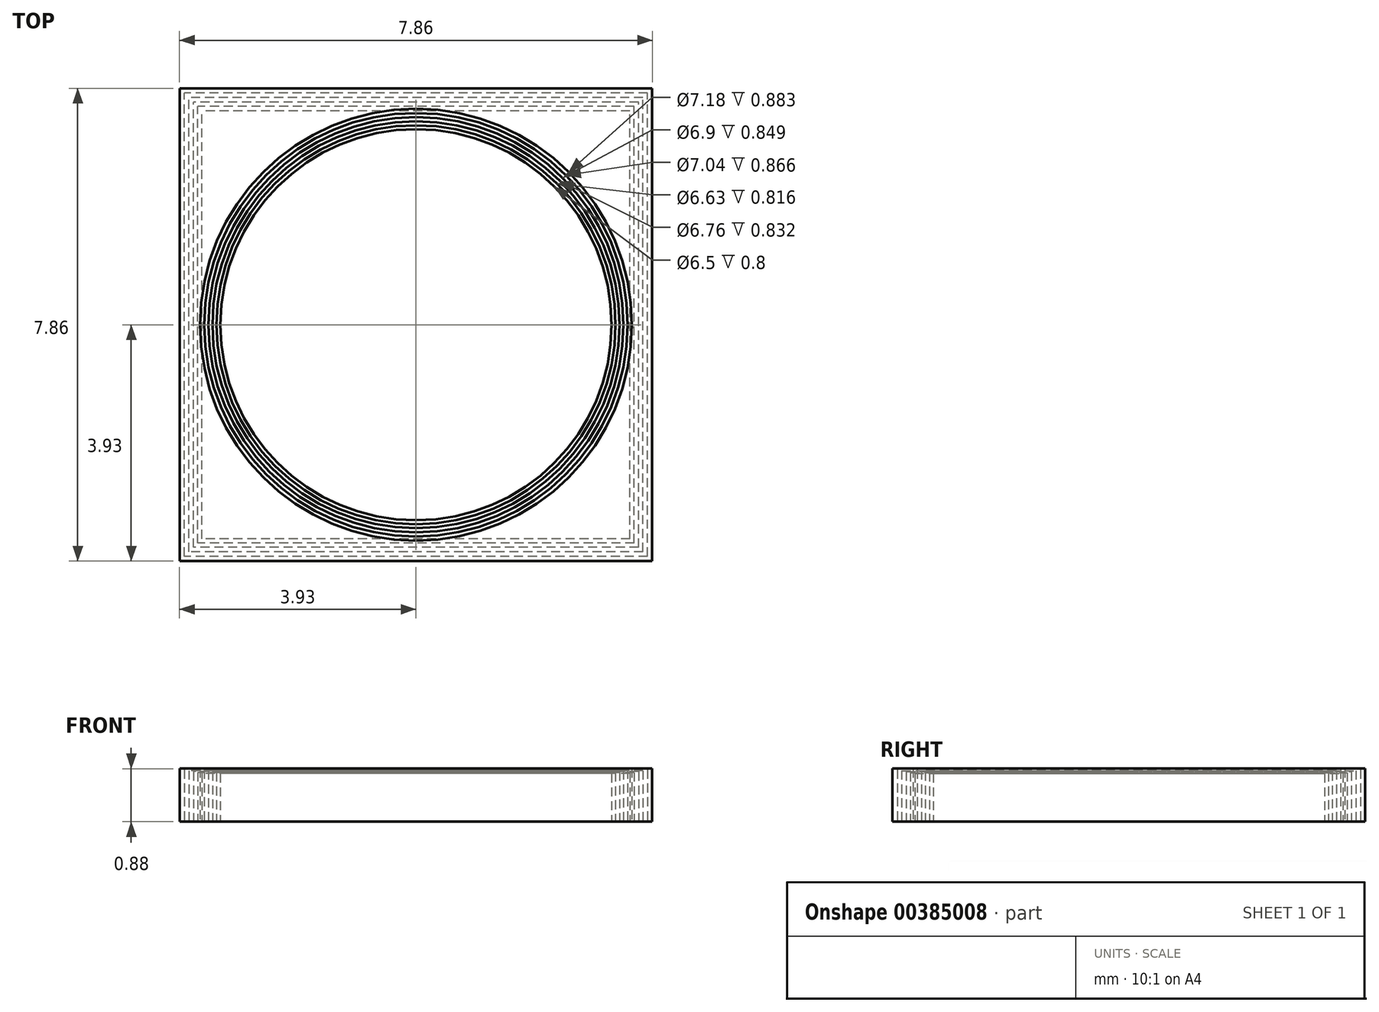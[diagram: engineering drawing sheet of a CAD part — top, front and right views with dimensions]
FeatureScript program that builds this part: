
annotation { "Feature Type Name" : "Feature", "Feature Type Description" : "" }
export const myFeature = defineFeature(function(context is Context, id is Id, definition is map)
    precondition{}
    {
        {
            var Q0;
            Q0=qCreatedBy(makeId("Top.planeOp"),FACE);
            var sketch = newSketch(context, id + "F0", { "sketchPlane" : qUnion([Q0])});
            skCircle(sketch, "E0", {"center": v(0, 0) * mm, "radius": 3.25 * mm});
            skLineSegment(sketch, "E1.bottom", {"start": v(3.56, -3.56) * mm, "end": v(-3.56, -3.56) * mm});
            skLineSegment(sketch, "E1.top", {"start": v(3.56, 3.56) * mm, "end": v(-3.56, 3.56) * mm});
            skLineSegment(sketch, "E1.left", {"start": v(3.56, -3.56) * mm, "end": v(3.56, 3.56) * mm});
            skLineSegment(sketch, "E1.right", {"start": v(-3.56, -3.56) * mm, "end": v(-3.56, 3.56) * mm});
            skSolve(sketch);
        }
        {
            var Q0;
            Q0=makeQuery(id+"F0.imprint","IMPRINT",FACE,{"disambiguationData":[TD([[makeQuery(id+"F0.imprint","IMPRINT",EDGE,{"derivedFrom":sQuery(id+"F0.wireOp",EDGE,"E0")}),-1.0]])]});
            extrude(context, id + "F1", {"entities" : qUnion([Q0]), "depth" : .8 * mm});
        }
        {
            var Q0;
            Q0=makeQuery(id+"F1.opExtrude","SWEPT_BODY",BODY,{"disambiguationData":[OSD([sQuery(id+"F0.wireOp",EDGE,"E0"),sQuery(id+"F0.wireOp",EDGE,"E1.bottom"),sQuery(id+"F0.wireOp",EDGE,"E1.top"),sQuery(id+"F0.wireOp",EDGE,"E1.left"),sQuery(id+"F0.wireOp",EDGE,"E1.right")])]});
            var Q1;
            Q1=sQuery(id+"F0.wireOp",VERTEX,"E0.center");
            transform(context, id + "F2", {"entities" : qUnion([Q0]), "transformType" : TransformType.SCALE_UNIFORMLY, "scale" : 1.02, "scalePoint" : qUnion([Q1]), "makeCopy" : true});
        }
        {
            var Q0;
            Q0=makeQuery(id+"F2.opPattern","COPY",BODY,{"derivedFrom":makeQuery(id+"F1.opExtrude","SWEPT_BODY",BODY,{"disambiguationData":[OSD([sQuery(id+"F0.wireOp",EDGE,"E0"),sQuery(id+"F0.wireOp",EDGE,"E1.bottom"),sQuery(id+"F0.wireOp",EDGE,"E1.top"),sQuery(id+"F0.wireOp",EDGE,"E1.left"),sQuery(id+"F0.wireOp",EDGE,"E1.right")])]}),"instanceName":"1"});
            var Q1;
            Q1=sQuery(id+"F0.wireOp",VERTEX,"E0.center");
            transform(context, id + "F3", {"entities" : qUnion([Q0]), "transformType" : TransformType.SCALE_UNIFORMLY, "scale" : 1.02, "scalePoint" : qUnion([Q1]), "makeCopy" : true});
        }
        {
            var Q0;
            Q0=makeQuery(id+"F3.opPattern","COPY",BODY,{"derivedFrom":makeQuery(id+"F2.opPattern","COPY",BODY,{"derivedFrom":makeQuery(id+"F1.opExtrude","SWEPT_BODY",BODY,{"disambiguationData":[OSD([sQuery(id+"F0.wireOp",EDGE,"E0"),sQuery(id+"F0.wireOp",EDGE,"E1.bottom"),sQuery(id+"F0.wireOp",EDGE,"E1.top"),sQuery(id+"F0.wireOp",EDGE,"E1.left"),sQuery(id+"F0.wireOp",EDGE,"E1.right")])]}),"instanceName":"1"}),"instanceName":"1"});
            var Q1;
            Q1=sQuery(id+"F0.wireOp",VERTEX,"E0.center");
            transform(context, id + "F4", {"entities" : qUnion([Q0]), "transformType" : TransformType.SCALE_UNIFORMLY, "scale" : 1.02, "scalePoint" : qUnion([Q1]), "makeCopy" : true});
        }
        {
            var Q0;
            Q0=makeQuery(id+"F4.opPattern","COPY",BODY,{"derivedFrom":makeQuery(id+"F3.opPattern","COPY",BODY,{"derivedFrom":makeQuery(id+"F2.opPattern","COPY",BODY,{"derivedFrom":makeQuery(id+"F1.opExtrude","SWEPT_BODY",BODY,{"disambiguationData":[OSD([sQuery(id+"F0.wireOp",EDGE,"E0"),sQuery(id+"F0.wireOp",EDGE,"E1.bottom"),sQuery(id+"F0.wireOp",EDGE,"E1.top"),sQuery(id+"F0.wireOp",EDGE,"E1.left"),sQuery(id+"F0.wireOp",EDGE,"E1.right")])]}),"instanceName":"1"}),"instanceName":"1"}),"instanceName":"1"});
            var Q1;
            Q1=sQuery(id+"F0.wireOp",VERTEX,"E0.center");
            transform(context, id + "F5", {"entities" : qUnion([Q0]), "transformType" : TransformType.SCALE_UNIFORMLY, "scale" : 1.02, "scalePoint" : qUnion([Q1]), "makeCopy" : true});
        }
        {
            var Q0;
            Q0=makeQuery(id+"F5.opPattern","COPY",BODY,{"derivedFrom":makeQuery(id+"F4.opPattern","COPY",BODY,{"derivedFrom":makeQuery(id+"F3.opPattern","COPY",BODY,{"derivedFrom":makeQuery(id+"F2.opPattern","COPY",BODY,{"derivedFrom":makeQuery(id+"F1.opExtrude","SWEPT_BODY",BODY,{"disambiguationData":[OSD([sQuery(id+"F0.wireOp",EDGE,"E0"),sQuery(id+"F0.wireOp",EDGE,"E1.bottom"),sQuery(id+"F0.wireOp",EDGE,"E1.top"),sQuery(id+"F0.wireOp",EDGE,"E1.left"),sQuery(id+"F0.wireOp",EDGE,"E1.right")])]}),"instanceName":"1"}),"instanceName":"1"}),"instanceName":"1"}),"instanceName":"1"});
            var Q1;
            Q1=sQuery(id+"F0.wireOp",VERTEX,"E0.center");
            transform(context, id + "F6", {"entities" : qUnion([Q0]), "transformType" : TransformType.SCALE_UNIFORMLY, "scale" : 1.02, "scalePoint" : qUnion([Q1]), "makeCopy" : true});
        }
    });
